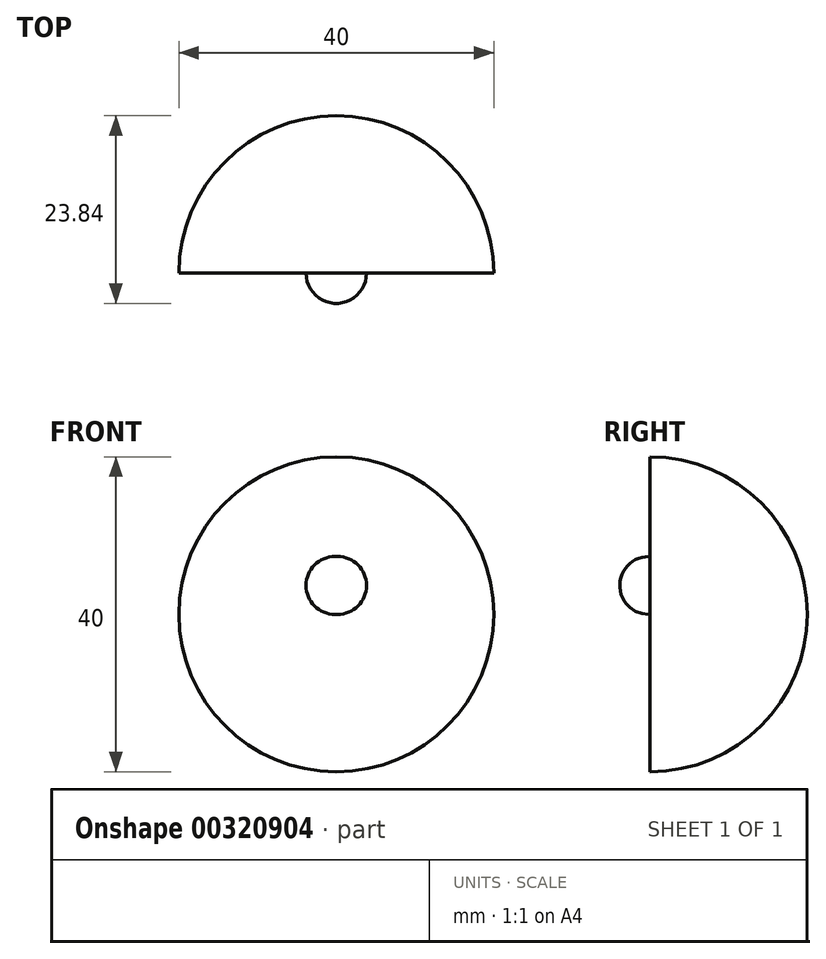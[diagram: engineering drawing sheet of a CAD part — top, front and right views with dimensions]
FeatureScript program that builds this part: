
annotation { "Feature Type Name" : "Feature", "Feature Type Description" : "" }
export const myFeature = defineFeature(function(context is Context, id is Id, definition is map)
    precondition{}
    {
        {
            var Q0;
            Q0=qCreatedBy(makeId("Front.planeOp"),FACE);
            var sketch = newSketch(context, id + "F0", { "sketchPlane" : qUnion([Q0])});
            skLineSegment(sketch, "E0", {"start": v(0, 0) * mm, "end": v(0, 40) * mm});
            skArc(sketch, "E1", {"start": v(0, 0) * mm, "mid": v(20, 20) * mm, "end": v(0, 40) * mm});
            skSolve(sketch);
        }
        {
            var Q0;
            Q0=makeQuery(id+"F0.imprint","IMPRINT",FACE,{"disambiguationData":[TD([[makeQuery(id+"F0.imprint","IMPRINT",EDGE,{"derivedFrom":sQuery(id+"F0.wireOp",EDGE,"E0")}),-1.0]])]});
            var Q1;
            Q1=sQuery(id+"F0.wireOp",EDGE,"E0");
            revolve(context, id + "F1", {"entities" : qUnion([Q0]), "axis" : qUnion([Q1]), "revolveType" : RevolveType.ONE_DIRECTION, "angle" : 180 * degree});
        }
        {
            var Q0;
            Q0=makeQuery(id+"F1.opRevolve","CAP_FACE",FACE,{"disambiguationData":[OSD([sQuery(id+"F0.wireOp",EDGE,"E0"),sQuery(id+"F0.wireOp",EDGE,"E1")])],"isStart":true});
            var sketch = newSketch(context, id + "F2", { "sketchPlane" : qUnion([Q0])});
            skLineSegment(sketch, "E2", {"start": v(0, 20) * mm, "end": v(0, 27.34) * mm});
            skArc(sketch, "E3", {"start": v(0, 20) * mm, "mid": v(3.84, 23.67) * mm, "end": v(0, 27.34) * mm});
            skSolve(sketch);
        }
        {
            var Q0;
            Q0 = qSketchRegion(id + "F2", true);
            var Q1;
            Q1=sQuery(id+"F2.wireOp",EDGE,"E2");
            revolve(context, id + "F3", {"operationType" : NewBodyOperationType.ADD, "entities" : qUnion([Q0]), "axis" : qUnion([Q1]), "revolveType" : RevolveType.FULL});
        }
    });
